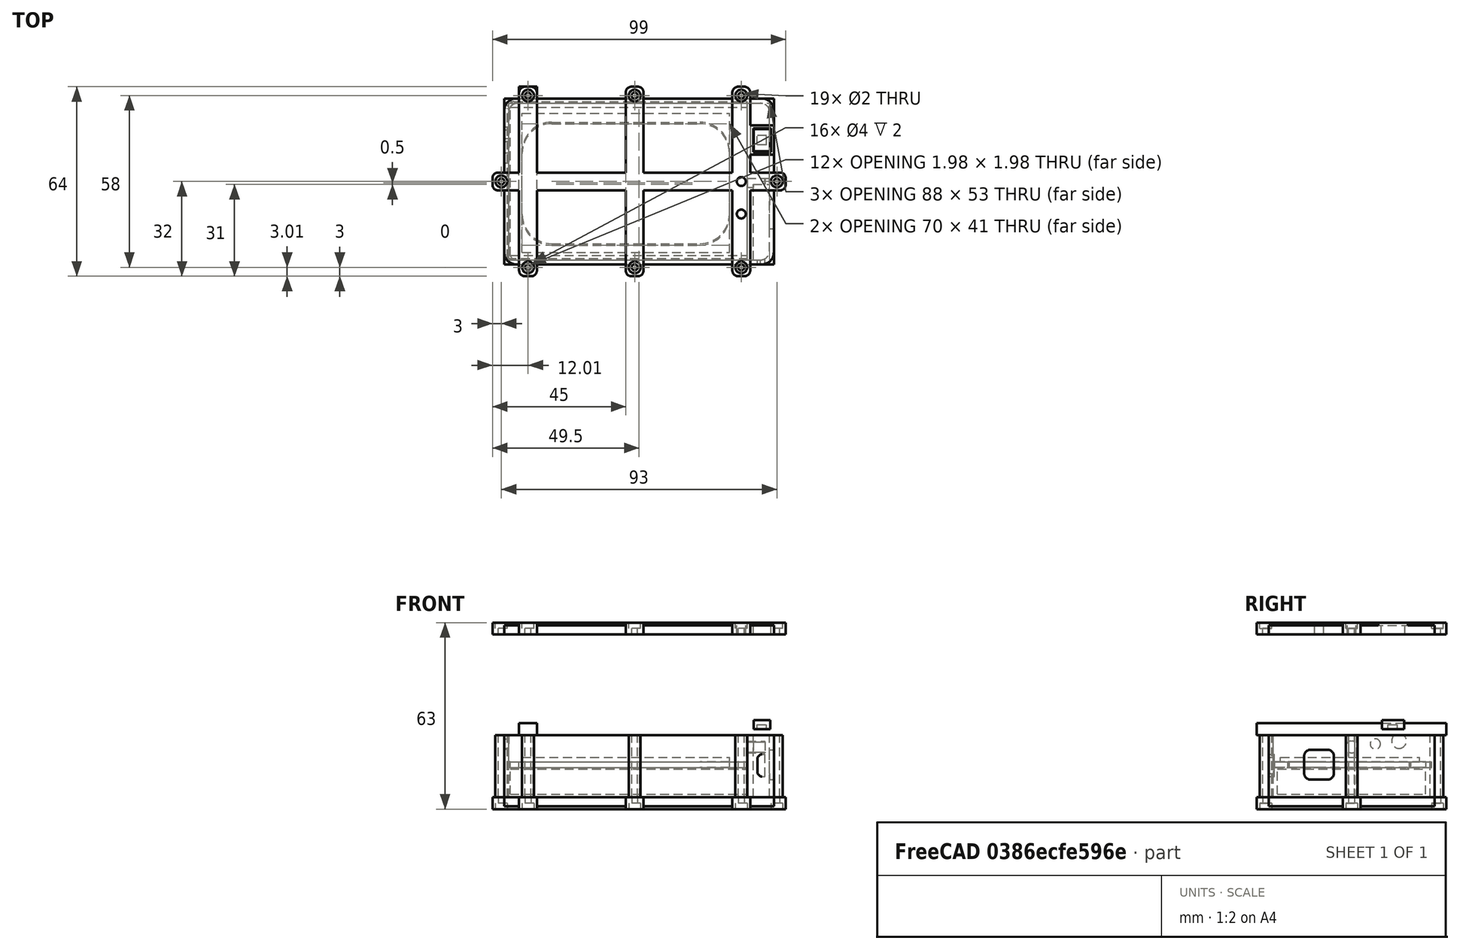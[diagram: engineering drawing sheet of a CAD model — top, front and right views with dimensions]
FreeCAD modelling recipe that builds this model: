
FCSTD DOCUMENT  (FreeCAD 0.20R29603 (Git))
Label: корпус
License: All rights reserved
LicenseURL: http://en.wikipedia.org/wiki/All_rights_reserved
objects: Part::Cylinder×43, Part::Fillet×35, Part::Cut×30, Part::Box×26, Part::MultiFuse×24, Part::FeaturePython×3, Part::Chamfer×1
note: 159 computed .brp shape members not serialized (recipe doc carries the construction recipe); baked Part::Feature solids carry a one-line shape summary decoded from their .brp

FEATURE [Part::Box] Box  label="Куб"
  AttacherType = Attacher::AttachEngine3D
  Height = 1.5
  Length = 70
  Placement = pos=(4,2,0) rot=(0,0,1;0rad)
  Width = 47
FEATURE [Part::Box] Box001  label="Куб001"
  AttacherType = Attacher::AttachEngine3D
  Height = 1.5
  Length = 17
  Width = 22
FEATURE [Part::Box] Box002  label="Куб002"
  AttacherType = Attacher::AttachEngine3D
  Height = 2.5
  Length = 7.5
  Placement = pos=(4.5,-4,1.5) rot=(0,0,1;0rad)
  Width = 11
FEATURE [Part::Chamfer] Chamfer
  Base = -> Box002
  Edges = 2 edges r=1: [Edge4,Edge8]
FEATURE [Part::MultiFuse] Fusion
  Placement = pos=(82,1,7) rot=(0,1,0;1.5708rad)
  Shapes = -> [Box001,Chamfer]
FEATURE [Part::Box] Box003  label="Куб003"
  AttacherType = Attacher::AttachEngine3D
  Height = 8.5
  Length = 80
  Placement = pos=(0,1,-11) rot=(0,0,1;0rad)
  Width = 50
FEATURE [Part::Box] Box004  label="Куб004"
  AttacherType = Attacher::AttachEngine3D
  Height = 21
  Length = 91
  Placement = pos=(-2,-2,-12) rot=(0,0,1;0rad)
  Width = 56
FEATURE [Part::Box] Box005  label="Куб005"
  AttacherType = Attacher::AttachEngine3D
  Height = 21
  Length = 88
  Placement = pos=(-0.5,-0.5,-12) rot=(0,0,1;0rad)
  Width = 53
FEATURE [Part::Cut] Cut
  Base = -> Box004
  Tool = -> Box005
FEATURE [Part::Box] Box006  label="Куб006"
  AttacherType = Attacher::AttachEngine3D
  Height = 21
  Length = 2
  Placement = pos=(80,-1,-12) rot=(0,0,1;0rad)
  Width = 26
FEATURE [Part::Box] Box007  label="Куб007"
  AttacherType = Attacher::AttachEngine3D
  Height = 21
  Length = 8
  Placement = pos=(80,25,-12) rot=(0,0,1;0rad)
  Width = 2
FEATURE [Part::Box] Box008  label="Куб008"
  AttacherType = Attacher::AttachEngine3D
  Height = 2
  Length = 81
  Placement = pos=(-1,0,-2) rot=(0,0,1;0rad)
  Width = 53
FEATURE [Part::Box] Box009  label="Куб009"
  AttacherType = Attacher::AttachEngine3D
  Height = 2
  Length = 70
  Placement = pos=(4,5,-2) rot=(0,0,1;0rad)
  Width = 41
FEATURE [Part::Fillet] Fillet
  Base = -> Box009
  Edges = 4 edges r=10: [Edge1,Edge3,Edge5,Edge7]
FEATURE [Part::Cut] Cut001
  Base = -> Box008
  Tool = -> Fillet
FEATURE [Part::Fillet] Fillet001
  Base = -> Cut
  Edges = 1 edges r=3: [Edge23]
FEATURE [Part::Fillet] Fillet002
  Base = -> Cut
  Edges = 1 edges r=3: [Edge23]
FEATURE [Part::Fillet] Fillet003
  Base = -> Fillet001
  Edges = 1 edges r=3: [Edge18]
FEATURE [Part::Fillet] Fillet004
  Base = -> Fillet001
  Edges = 1 edges r=3: [Edge18]
FEATURE [Part::Fillet] Fillet005
  Base = -> Fillet004
  Edges = 1 edges r=3: [Edge16]
FEATURE [Part::Fillet] Fillet006
  Base = -> Fillet005
  Edges = 1 edges r=3: [Edge20]
FEATURE [Part::Fillet] Fillet007
  Base = -> Fillet006
  Edges = 1 edges r=4: [Edge30]
FEATURE [Part::Fillet] Fillet008
  Base = -> Cut001
  Edges = 1 edges r=2.3: [Edge3]
FEATURE [Part::Fillet] Fillet009
  Base = -> Cut001
  Edges = 1 edges r=4: [Edge3]
  Placement = pos=(0,-0.5,0) rot=(0,0,1;0rad)
FEATURE [Part::Fillet] Fillet010
  Base = -> Fillet007
  Edges = 1 edges r=4: [Edge14]
FEATURE [Part::Fillet] Fillet011
  Base = -> Fillet007
  Edges = 1 edges r=4: [Edge14]
FEATURE [Part::Fillet] Fillet012
  Base = -> Fillet011
  Edges = 1 edges r=4: [Edge23]
FEATURE [Part::Fillet] Fillet013
  Base = -> Fillet012
  Edges = 1 edges r=4: [Edge24]
FEATURE [Part::Cut] Cut002
  Base = -> Fillet013
  Tool = -> Fusion
FEATURE [Part::Cylinder] Cylinder  label="Цилиндр"
  Angle = 360
  AttacherType = Attacher::AttachEngine3D
  FirstAngle = 0
  Height = 10
  Placement = pos=(-6,42,7) rot=(0,1,0;1.5708rad)
  Radius = 2.5
  SecondAngle = 0
FEATURE [Part::Cut] Cut003
  Base = -> Cut002
  Tool = -> Cylinder
FEATURE [Part::Cylinder] Cylinder001  label="Цилиндр001"
  Angle = 360
  AttacherType = Attacher::AttachEngine3D
  FirstAngle = 0
  Height = 10
  Placement = pos=(-4,34,6) rot=(0,1,0;1.5708rad)
  Radius = 1.75
  SecondAngle = 0
FEATURE [Part::Cut] Cut004
  Base = -> Cut003
  Tool = -> Cylinder001
FEATURE [Part::Box] Box010  label="Куб010"
  AttacherType = Attacher::AttachEngine3D
  Height = 10
  Length = 1.5
  Placement = pos=(87.5,10,-6) rot=(0,0,1;0rad)
  Width = 10
FEATURE [Part::MultiFuse] Fusion001
  Shapes = -> [Box006,Box007,Cut004,Fillet009]
FEATURE [Part::Fillet] Fillet014
  Base = -> Box010
  Edges = 4 edges r=2: [Edge9,Edge10,Edge11,Edge12]
FEATURE [Part::Box] Box011  label="Куб011"
  AttacherType = Attacher::AttachEngine3D
  Height = 10
  Length = 1.5
  Placement = pos=(87.5,10,-6) rot=(0,0,1;0rad)
  Width = 10
FEATURE [Part::Fillet] Fillet015
  Base = -> Box011
  Edges = 4 edges r=2: [Edge9,Edge10,Edge11,Edge12]
FEATURE [Part::Cut] Cut005
  Base = -> Fusion001
  Tool = -> Fillet014
FEATURE [Part::Cylinder] Cylinder002  label="Цилиндр002"
  Angle = 360
  AttacherType = Attacher::AttachEngine3D
  FirstAngle = 0
  Height = 10
  Placement = pos=(76,26,5) rot=(0,1,0;1.5708rad)
  Radius = 2
  SecondAngle = 0
FEATURE [Part::Cut] Cut006
  Base = -> Cut005
  Tool = -> Cylinder002
FEATURE [Part::Cylinder] Cylinder003  label="Цилиндр003"
  Angle = 360
  AttacherType = Attacher::AttachEngine3D
  FirstAngle = 0
  Height = 21
  Placement = pos=(6,-3,-12) rot=(0,0,1;0rad)
  Radius = 2
  SecondAngle = 0
FEATURE [Part::Cylinder] Cylinder004  label="Цилиндр004"
  Angle = 360
  AttacherType = Attacher::AttachEngine3D
  FirstAngle = 0
  Height = 21
  Placement = pos=(6,-3,-12) rot=(0,0,1;0rad)
  Radius = 1
  SecondAngle = 0
FEATURE [Part::Cut] Cut007
  Base = -> Cylinder003
  Tool = -> Cylinder004
FEATURE [Part::FeaturePython] Array  # Draft array (typed FeaturePython)
  AlwaysSyncPlacement = false
  Angle = 360
  ArrayType = 0
  Axis = (0,0,1)
  Base = -> Cut007
  Center = (0,0,0)
  Count = 3
  ExpandArray = false
  Fuse = false
  IntervalAxis = (0,0,0)
  IntervalX = (36,0,0)
  IntervalY = (0,100,0)
  IntervalZ = (0,0,100)
  NumberCircles = 3
  NumberPolar = 5
  NumberX = 3
  NumberY = 1
  NumberZ = 1
  PlacementList = 3 placements: arithmetic series from (0,0,0) step (36,0,0) to (72,0,0)
  RadialDistance = 50
  ScaleList = (3) [(1,1,1),(1,1,1),(1,1,1)]
  Symmetry = 1
  TangentialDistance = 25
FEATURE [Part::Cylinder] Cylinder005  label="Цилиндр005"
  Angle = 360
  AttacherType = Attacher::AttachEngine3D
  FirstAngle = 0
  Height = 21
  Placement = pos=(6,-3,-12) rot=(0,0,1;0rad)
  Radius = 1
  SecondAngle = 0
FEATURE [Part::Cylinder] Cylinder006  label="Цилиндр006"
  Angle = 360
  AttacherType = Attacher::AttachEngine3D
  FirstAngle = 0
  Height = 21
  Placement = pos=(6,-3,-12) rot=(0,0,1;0rad)
  Radius = 2
  SecondAngle = 0
FEATURE [Part::Cut] Cut008
  Base = -> Cylinder006
  Tool = -> Cylinder005
FEATURE [Part::FeaturePython] Array001  # Draft array (typed FeaturePython)
  AlwaysSyncPlacement = false
  Angle = 360
  ArrayType = 0
  Axis = (0,0,1)
  Base = -> Cut008
  Center = (0,0,0)
  Count = 3
  ExpandArray = false
  Fuse = false
  IntervalAxis = (0,0,0)
  IntervalX = (36,0,0)
  IntervalY = (0,100,0)
  IntervalZ = (0,0,100)
  NumberCircles = 3
  NumberPolar = 5
  NumberX = 3
  NumberY = 1
  NumberZ = 1
  Placement = pos=(0,58,0) rot=(0,0,1;0rad)
  PlacementList = 3 placements: arithmetic series from (0,0,0) step (36,0,0) to (72,0,0)
  RadialDistance = 50
  ScaleList = (3) [(1,1,1),(1,1,1),(1,1,1)]
  Symmetry = 1
  TangentialDistance = 25
FEATURE [Part::Cylinder] Cylinder007  label="Цилиндр007"
  Angle = 360
  AttacherType = Attacher::AttachEngine3D
  FirstAngle = 0
  Height = 21
  Placement = pos=(6,-3,-12) rot=(0,0,1;0rad)
  Radius = 1
  SecondAngle = 0
FEATURE [Part::Cylinder] Cylinder008  label="Цилиндр008"
  Angle = 360
  AttacherType = Attacher::AttachEngine3D
  FirstAngle = 0
  Height = 21
  Placement = pos=(6,-3,-12) rot=(0,0,1;0rad)
  Radius = 2
  SecondAngle = 0
FEATURE [Part::Cut] Cut009
  Base = -> Cylinder008
  Placement = pos=(-9,29,0) rot=(0,0,1;0rad)
  Tool = -> Cylinder007
FEATURE [Part::FeaturePython] Array002  # Draft array (typed FeaturePython)
  AlwaysSyncPlacement = false
  Angle = 360
  ArrayType = 0
  Axis = (0,0,1)
  Base = -> Cut009
  Center = (0,0,0)
  Count = 2
  ExpandArray = false
  Fuse = false
  IntervalAxis = (0,0,0)
  IntervalX = (93,0,0)
  IntervalY = (0,100,0)
  IntervalZ = (0,0,100)
  NumberCircles = 3
  NumberPolar = 5
  NumberX = 2
  NumberY = 1
  NumberZ = 1
  PlacementList = 2 placements: [(-9,29,0),(84,29,0)]
  RadialDistance = 50
  ScaleList = (2) [(1,1,1),(1,1,1)]
  Symmetry = 1
  TangentialDistance = 25
FEATURE [Part::MultiFuse] Fusion002
  Shapes = -> [Cut006,Array,Array001,Array002]
FEATURE [Part::Box] Box012  label="Куб012"
  AttacherType = Attacher::AttachEngine3D
  Height = 3
  Length = 91
  Placement = pos=(-2,-2,9) rot=(0,0,1;0rad)
  Width = 56
FEATURE [Part::Fillet] Fillet016
  Base = -> Box012
  Edges = 4 edges r=4: [Edge1,Edge3,Edge5,Edge7]
FEATURE [Part::Box] Box013  label="Куб013"
  AttacherType = Attacher::AttachEngine3D
  Height = 4
  Length = 6
  Placement = pos=(3,-6,9) rot=(0,0,1;0rad)
  Width = 64
FEATURE [Part::Fillet] Fillet017
  Base = -> Box013
  Edges = 2 edges r=1.9: [Edge1,Edge5]
FEATURE [Part::Fillet] Fillet018
  Base = -> Box013
  Edges = 2 edges r=1.9: [Edge1,Edge5]
FEATURE [Part::Fillet] Fillet019
  Base = -> Fillet018
  Edges = 2 edges r=1.9: [Edge4,Edge13]
FEATURE [Part::Box] Box014  label="Куб014"
  AttacherType = Attacher::AttachEngine3D
  Height = 4
  Length = 6
  Placement = pos=(3,-6,9) rot=(0,0,1;0rad)
  Width = 64
FEATURE [Part::Fillet] Fillet021
  Base = -> Box014
  Edges = 2 edges r=1.9: [Edge1,Edge5]
FEATURE [Part::Fillet] Fillet020
  Base = -> Fillet021
  Edges = 2 edges r=1.9: [Edge4,Edge13]
  Placement = pos=(36,0,0) rot=(0,0,1;0rad)
FEATURE [Part::Box] Box015  label="Куб015"
  AttacherType = Attacher::AttachEngine3D
  Height = 4
  Length = 6
  Placement = pos=(3,-6,9) rot=(0,0,1;0rad)
  Width = 64
FEATURE [Part::Fillet] Fillet022
  Base = -> Box015
  Edges = 2 edges r=1.9: [Edge1,Edge5]
FEATURE [Part::Fillet] Fillet023
  Base = -> Fillet022
  Edges = 2 edges r=1.9: [Edge4,Edge13]
  Placement = pos=(72,0,0) rot=(0,0,1;0rad)
FEATURE [Part::Box] Box016  label="Куб016"
  AttacherType = Attacher::AttachEngine3D
  Height = 4
  Length = 6
  Placement = pos=(3,-6,9) rot=(0,0,1;0rad)
  Width = 99
FEATURE [Part::Fillet] Fillet024
  Base = -> Box016
  Edges = 2 edges r=1.9: [Edge1,Edge5]
FEATURE [Part::Fillet] Fillet025
  Base = -> Fillet024
  Edges = 2 edges r=1.9: [Edge4,Edge13]
  Placement = pos=(87,20,0) rot=(0,0,1;1.5708rad)
FEATURE [Part::Cylinder] Cylinder009  label="Цилиндр009"
  Angle = 360
  AttacherType = Attacher::AttachEngine3D
  FirstAngle = 0
  Height = 10
  Placement = pos=(6,-3,5) rot=(0,0,1;0rad)
  Radius = 1
  SecondAngle = 0
FEATURE [Part::Cylinder] Cylinder010  label="Цилиндр010"
  Angle = 360
  AttacherType = Attacher::AttachEngine3D
  FirstAngle = 0
  Height = 2
  Placement = pos=(6,-3,11) rot=(0,0,1;0rad)
  Radius = 2
  SecondAngle = 0
FEATURE [Part::MultiFuse] Fusion003
  Shapes = -> [Cylinder009,Cylinder010]
FEATURE [Part::Cylinder] Cylinder011  label="Цилиндр011"
  Angle = 360
  AttacherType = Attacher::AttachEngine3D
  FirstAngle = 0
  Height = 2
  Placement = pos=(6,-3,11) rot=(0,0,1;0rad)
  Radius = 2
  SecondAngle = 0
FEATURE [Part::Cylinder] Cylinder012  label="Цилиндр012"
  Angle = 360
  AttacherType = Attacher::AttachEngine3D
  FirstAngle = 0
  Height = 10
  Placement = pos=(6,-3,5) rot=(0,0,1;0rad)
  Radius = 1
  SecondAngle = 0
FEATURE [Part::MultiFuse] Fusion004
  Placement = pos=(36,0,0) rot=(0,0,1;0rad)
  Shapes = -> [Cylinder012,Cylinder011]
FEATURE [Part::Cylinder] Cylinder013  label="Цилиндр013"
  Angle = 360
  AttacherType = Attacher::AttachEngine3D
  FirstAngle = 0
  Height = 2
  Placement = pos=(6,-3,11) rot=(0,0,1;0rad)
  Radius = 2
  SecondAngle = 0
FEATURE [Part::Cylinder] Cylinder014  label="Цилиндр014"
  Angle = 360
  AttacherType = Attacher::AttachEngine3D
  FirstAngle = 0
  Height = 10
  Placement = pos=(6,-3,5) rot=(0,0,1;0rad)
  Radius = 1
  SecondAngle = 0
FEATURE [Part::MultiFuse] Fusion005
  Placement = pos=(72,0,0) rot=(0,0,1;0rad)
  Shapes = -> [Cylinder014,Cylinder013]
FEATURE [Part::Cylinder] Cylinder015  label="Цилиндр015"
  Angle = 360
  AttacherType = Attacher::AttachEngine3D
  FirstAngle = 0
  Height = 2
  Placement = pos=(6,-3,11) rot=(0,0,1;0rad)
  Radius = 2
  SecondAngle = 0
FEATURE [Part::Cylinder] Cylinder016  label="Цилиндр016"
  Angle = 360
  AttacherType = Attacher::AttachEngine3D
  FirstAngle = 0
  Height = 10
  Placement = pos=(6,-3,5) rot=(0,0,1;0rad)
  Radius = 1
  SecondAngle = 0
FEATURE [Part::Cylinder] Cylinder017  label="Цилиндр017"
  Angle = 360
  AttacherType = Attacher::AttachEngine3D
  FirstAngle = 0
  Height = 2
  Placement = pos=(6,-3,11) rot=(0,0,1;0rad)
  Radius = 2
  SecondAngle = 0
FEATURE [Part::Cylinder] Cylinder018  label="Цилиндр018"
  Angle = 360
  AttacherType = Attacher::AttachEngine3D
  FirstAngle = 0
  Height = 10
  Placement = pos=(6,-3,5) rot=(0,0,1;0rad)
  Radius = 1
  SecondAngle = 0
FEATURE [Part::MultiFuse] Fusion006
  Placement = pos=(36,58,0) rot=(0,0,1;0rad)
  Shapes = -> [Cylinder018,Cylinder017]
FEATURE [Part::Cylinder] Cylinder019  label="Цилиндр019"
  Angle = 360
  AttacherType = Attacher::AttachEngine3D
  FirstAngle = 0
  Height = 10
  Placement = pos=(6,-3,5) rot=(0,0,1;0rad)
  Radius = 1
  SecondAngle = 0
FEATURE [Part::MultiFuse] Fusion007
  Placement = pos=(0,58,0) rot=(0,0,1;0rad)
  Shapes = -> [Cylinder019,Cylinder015]
FEATURE [Part::Cylinder] Cylinder020  label="Цилиндр020"
  Angle = 360
  AttacherType = Attacher::AttachEngine3D
  FirstAngle = 0
  Height = 2
  Placement = pos=(6,-3,11) rot=(0,0,1;0rad)
  Radius = 2
  SecondAngle = 0
FEATURE [Part::MultiFuse] Fusion008
  Placement = pos=(72,58,0) rot=(0,0,1;0rad)
  Shapes = -> [Cylinder016,Cylinder020]
FEATURE [Part::Cylinder] Cylinder021  label="Цилиндр021"
  Angle = 360
  AttacherType = Attacher::AttachEngine3D
  FirstAngle = 0
  Height = 2
  Placement = pos=(6,-3,11) rot=(0,0,1;0rad)
  Radius = 2
  SecondAngle = 0
FEATURE [Part::Cylinder] Cylinder022  label="Цилиндр022"
  Angle = 360
  AttacherType = Attacher::AttachEngine3D
  FirstAngle = 0
  Height = 10
  Placement = pos=(6,-3,5) rot=(0,0,1;0rad)
  Radius = 1
  SecondAngle = 0
FEATURE [Part::MultiFuse] Fusion009
  Placement = pos=(84,29,0) rot=(0,0,1;0rad)
  Shapes = -> [Cylinder022,Cylinder021]
FEATURE [Part::Cylinder] Cylinder023  label="Цилиндр023"
  Angle = 360
  AttacherType = Attacher::AttachEngine3D
  FirstAngle = 0
  Height = 2
  Placement = pos=(6,-3,11) rot=(0,0,1;0rad)
  Radius = 2
  SecondAngle = 0
FEATURE [Part::Cylinder] Cylinder024  label="Цилиндр024"
  Angle = 360
  AttacherType = Attacher::AttachEngine3D
  FirstAngle = 0
  Height = 10
  Placement = pos=(6,-3,5) rot=(0,0,1;0rad)
  Radius = 1
  SecondAngle = 0
FEATURE [Part::MultiFuse] Fusion010
  Placement = pos=(-9,29,0) rot=(0,0,1;0rad)
  Shapes = -> [Cylinder024,Cylinder023]
FEATURE [Part::MultiFuse] Fusion011
  Shapes = -> [Fillet025,Fillet023,Fillet020,Fillet019]
FEATURE [Part::MultiFuse] Fusion012
  Shapes = -> [Fillet016,Fusion011]
FEATURE [Part::Cut] Cut010
  Base = -> Fusion012
  Tool = -> Fusion010
FEATURE [Part::Cut] Cut011
  Base = -> Cut010
  Tool = -> Fusion009
FEATURE [Part::Cut] Cut012
  Base = -> Cut011
  Tool = -> Fusion008
FEATURE [Part::Cut] Cut013
  Base = -> Cut012
  Tool = -> Fusion007
FEATURE [Part::Cut] Cut014
  Base = -> Cut013
  Tool = -> Fusion006
FEATURE [Part::Cut] Cut015
  Base = -> Cut014
  Tool = -> Fusion005
FEATURE [Part::Cut] Cut016
  Base = -> Cut015
  Tool = -> Fusion004
FEATURE [Part::Cut] Cut017
  Base = -> Cut016
  Tool = -> Fusion003
FEATURE [Part::Box] Box017  label="Куб017"
  AttacherType = Attacher::AttachEngine3D
  Height = 4
  Length = 6
  Placement = pos=(3,-6,9) rot=(0,0,1;0rad)
  Width = 64
FEATURE [Part::Fillet] Fillet026
  Base = -> Box017
  Edges = 2 edges r=1.9: [Edge1,Edge5]
FEATURE [Part::Box] Box018  label="Куб018"
  AttacherType = Attacher::AttachEngine3D
  Height = 4
  Length = 6
  Placement = pos=(3,-6,9) rot=(0,0,1;0rad)
  Width = 64
FEATURE [Part::Box] Box019  label="Куб019"
  AttacherType = Attacher::AttachEngine3D
  Height = 3
  Length = 91
  Placement = pos=(-2,-2,9) rot=(0,0,1;0rad)
  Width = 56
FEATURE [Part::Fillet] Fillet028
  Base = -> Box019
  Edges = 4 edges r=4: [Edge1,Edge3,Edge5,Edge7]
FEATURE [Part::Fillet] Fillet030
  Base = -> Box018
  Edges = 2 edges r=1.9: [Edge1,Edge5]
FEATURE [Part::Fillet] Fillet027
  Base = -> Fillet030
  Edges = 2 edges r=1.9: [Edge4,Edge13]
FEATURE [Part::Fillet] Fillet031
  Base = -> Fillet026
  Edges = 2 edges r=1.9: [Edge4,Edge13]
  Placement = pos=(36,0,0) rot=(0,0,1;0rad)
FEATURE [Part::Cylinder] Cylinder025  label="Цилиндр025"
  Angle = 360
  AttacherType = Attacher::AttachEngine3D
  FirstAngle = 0
  Height = 2
  Placement = pos=(6,-3,11) rot=(0,0,1;0rad)
  Radius = 2
  SecondAngle = 0
FEATURE [Part::Cylinder] Cylinder026  label="Цилиндр026"
  Angle = 360
  AttacherType = Attacher::AttachEngine3D
  FirstAngle = 0
  Height = 2
  Placement = pos=(6,-3,11) rot=(0,0,1;0rad)
  Radius = 2
  SecondAngle = 0
FEATURE [Part::Cylinder] Cylinder027  label="Цилиндр027"
  Angle = 360
  AttacherType = Attacher::AttachEngine3D
  FirstAngle = 0
  Height = 10
  Placement = pos=(6,-3,5) rot=(0,0,1;0rad)
  Radius = 1
  SecondAngle = 0
FEATURE [Part::MultiFuse] Fusion017
  Placement = pos=(84,29,0) rot=(0,0,1;0rad)
  Shapes = -> [Cylinder027,Cylinder025]
FEATURE [Part::Cylinder] Cylinder028  label="Цилиндр028"
  Angle = 360
  AttacherType = Attacher::AttachEngine3D
  FirstAngle = 0
  Height = 2
  Placement = pos=(6,-3,11) rot=(0,0,1;0rad)
  Radius = 2
  SecondAngle = 0
FEATURE [Part::Cylinder] Cylinder029  label="Цилиндр029"
  Angle = 360
  AttacherType = Attacher::AttachEngine3D
  FirstAngle = 0
  Height = 10
  Placement = pos=(6,-3,5) rot=(0,0,1;0rad)
  Radius = 1
  SecondAngle = 0
FEATURE [Part::MultiFuse] Fusion014
  Placement = pos=(-9,29,0) rot=(0,0,1;0rad)
  Shapes = -> [Cylinder029,Cylinder028]
FEATURE [Part::Cylinder] Cylinder030  label="Цилиндр030"
  Angle = 360
  AttacherType = Attacher::AttachEngine3D
  FirstAngle = 0
  Height = 2
  Placement = pos=(6,-3,11) rot=(0,0,1;0rad)
  Radius = 2
  SecondAngle = 0
FEATURE [Part::Cylinder] Cylinder031  label="Цилиндр031"
  Angle = 360
  AttacherType = Attacher::AttachEngine3D
  FirstAngle = 0
  Height = 10
  Placement = pos=(6,-3,5) rot=(0,0,1;0rad)
  Radius = 1
  SecondAngle = 0
FEATURE [Part::Box] Box020  label="Куб020"
  AttacherType = Attacher::AttachEngine3D
  Height = 4
  Length = 6
  Placement = pos=(3,-6,9) rot=(0,0,1;0rad)
  Width = 99
FEATURE [Part::Fillet] Fillet034
  Base = -> Box020
  Edges = 2 edges r=1.9: [Edge1,Edge5]
FEATURE [Part::Fillet] Fillet033
  Base = -> Fillet034
  Edges = 2 edges r=1.9: [Edge4,Edge13]
  Placement = pos=(87,20,0) rot=(0,0,1;1.5708rad)
FEATURE [Part::Cylinder] Cylinder032  label="Цилиндр032"
  Angle = 360
  AttacherType = Attacher::AttachEngine3D
  FirstAngle = 0
  Height = 2
  Placement = pos=(6,-3,11) rot=(0,0,1;0rad)
  Radius = 2
  SecondAngle = 0
FEATURE [Part::Cylinder] Cylinder033  label="Цилиндр033"
  Angle = 360
  AttacherType = Attacher::AttachEngine3D
  FirstAngle = 0
  Height = 10
  Placement = pos=(6,-3,5) rot=(0,0,1;0rad)
  Radius = 1
  SecondAngle = 0
FEATURE [Part::MultiFuse] Fusion018
  Placement = pos=(36,0,0) rot=(0,0,1;0rad)
  Shapes = -> [Cylinder033,Cylinder032]
FEATURE [Part::Cylinder] Cylinder034  label="Цилиндр034"
  Angle = 360
  AttacherType = Attacher::AttachEngine3D
  FirstAngle = 0
  Height = 10
  Placement = pos=(6,-3,5) rot=(0,0,1;0rad)
  Radius = 1
  SecondAngle = 0
FEATURE [Part::MultiFuse] Fusion019
  Shapes = -> [Cylinder034,Cylinder030]
FEATURE [Part::Cylinder] Cylinder035  label="Цилиндр035"
  Angle = 360
  AttacherType = Attacher::AttachEngine3D
  FirstAngle = 0
  Height = 2
  Placement = pos=(6,-3,11) rot=(0,0,1;0rad)
  Radius = 2
  SecondAngle = 0
FEATURE [Part::MultiFuse] Fusion022
  Placement = pos=(72,0,0) rot=(0,0,1;0rad)
  Shapes = -> [Cylinder031,Cylinder035]
FEATURE [Part::Cylinder] Cylinder036  label="Цилиндр036"
  Angle = 360
  AttacherType = Attacher::AttachEngine3D
  FirstAngle = 0
  Height = 2
  Placement = pos=(6,-3,11) rot=(0,0,1;0rad)
  Radius = 2
  SecondAngle = 0
FEATURE [Part::Cylinder] Cylinder037  label="Цилиндр037"
  Angle = 360
  AttacherType = Attacher::AttachEngine3D
  FirstAngle = 0
  Height = 10
  Placement = pos=(6,-3,5) rot=(0,0,1;0rad)
  Radius = 1
  SecondAngle = 0
FEATURE [Part::MultiFuse] Fusion015
  Placement = pos=(72,58,0) rot=(0,0,1;0rad)
  Shapes = -> [Cylinder037,Cylinder026]
FEATURE [Part::Cylinder] Cylinder038  label="Цилиндр038"
  Angle = 360
  AttacherType = Attacher::AttachEngine3D
  FirstAngle = 0
  Height = 10
  Placement = pos=(6,-3,5) rot=(0,0,1;0rad)
  Radius = 1
  SecondAngle = 0
FEATURE [Part::Cylinder] Cylinder039  label="Цилиндр039"
  Angle = 360
  AttacherType = Attacher::AttachEngine3D
  FirstAngle = 0
  Height = 2
  Placement = pos=(6,-3,11) rot=(0,0,1;0rad)
  Radius = 2
  SecondAngle = 0
FEATURE [Part::MultiFuse] Fusion020
  Placement = pos=(36,58,0) rot=(0,0,1;0rad)
  Shapes = -> [Cylinder038,Cylinder039]
FEATURE [Part::Box] Box021  label="Куб021"
  AttacherType = Attacher::AttachEngine3D
  Height = 4
  Length = 6
  Placement = pos=(3,-6,9) rot=(0,0,1;0rad)
  Width = 64
FEATURE [Part::Fillet] Fillet029
  Base = -> Box021
  Edges = 2 edges r=1.9: [Edge1,Edge5]
FEATURE [Part::Fillet] Fillet032
  Base = -> Fillet029
  Edges = 2 edges r=1.9: [Edge4,Edge13]
  Placement = pos=(72,0,0) rot=(0,0,1;0rad)
FEATURE [Part::MultiFuse] Fusion016
  Shapes = -> [Fillet033,Fillet032,Fillet031,Fillet027]
FEATURE [Part::MultiFuse] Fusion013
  Shapes = -> [Fillet028,Fusion016]
FEATURE [Part::Cut] Cut020
  Base = -> Fusion013
  Tool = -> Fusion014
FEATURE [Part::Cut] Cut025
  Base = -> Cut020
  Tool = -> Fusion017
FEATURE [Part::Cut] Cut022
  Base = -> Cut025
  Tool = -> Fusion015
FEATURE [Part::Cylinder] Cylinder040  label="Цилиндр040"
  Angle = 360
  AttacherType = Attacher::AttachEngine3D
  FirstAngle = 0
  Height = 10
  Placement = pos=(6,-3,5) rot=(0,0,1;0rad)
  Radius = 1
  SecondAngle = 0
FEATURE [Part::MultiFuse] Fusion021
  Placement = pos=(0,58,0) rot=(0,0,1;0rad)
  Shapes = -> [Cylinder040,Cylinder036]
FEATURE [Part::Cut] Cut019
  Base = -> Cut022
  Tool = -> Fusion021
FEATURE [Part::Cut] Cut024
  Base = -> Cut019
  Tool = -> Fusion020
FEATURE [Part::Cut] Cut023
  Base = -> Cut024
  Tool = -> Fusion022
FEATURE [Part::Cut] Cut021
  Base = -> Cut023
  Tool = -> Fusion018
FEATURE [Part::Cut] Cut018
  Base = -> Cut021
  Placement = pos=(0,52,-3) rot=(1,0,0;3.14159rad)
  Tool = -> Fusion019
FEATURE [Part::Cylinder] Cylinder041  label="Цилиндр041"
  Angle = 360
  AttacherType = Attacher::AttachEngine3D
  FirstAngle = 0
  Height = 10
  Placement = pos=(78,15,3) rot=(0,0,1;0rad)
  Radius = 1.5
  SecondAngle = 0
FEATURE [Part::Cylinder] Cylinder042  label="Цилиндр042"
  Angle = 360
  AttacherType = Attacher::AttachEngine3D
  FirstAngle = 0
  Height = 10
  Placement = pos=(78,26,3) rot=(0,0,1;0rad)
  Radius = 1.5
  SecondAngle = 0
FEATURE [Part::Cut] Cut026
  Base = -> Cut017
  Tool = -> Cylinder041
FEATURE [Part::Cut] Cut027
  Base = -> Cut026
  Tool = -> Cylinder042
FEATURE [Part::Box] Box022  label="Куб022"
  AttacherType = Attacher::AttachEngine3D
  Height = 4
  Length = 8
  Placement = pos=(81,35,9) rot=(0,0,1;0rad)
  Width = 10
FEATURE [Part::Box] Box023  label="Куб023"
  AttacherType = Attacher::AttachEngine3D
  Height = 4
  Length = 6
  Placement = pos=(82,36,9) rot=(0,0,1;0rad)
  Width = 8
FEATURE [Part::MultiFuse] Fusion023
  Shapes = -> [Box022,Cut027]
FEATURE [Part::Cut] Cut028
  Base = -> Fusion023
  Placement = pos=(0,0,34) rot=(0,0,1;0rad)
  Tool = -> Box023
FEATURE [Part::Box] Box024  label="Куб024"
  AttacherType = Attacher::AttachEngine3D
  Height = 3
  Length = 5.5
  Placement = pos=(82.25,36.25,18) rot=(0,0,1;0rad)
  Width = 7.5
FEATURE [Part::Box] Box025  label="Куб025"
  AttacherType = Attacher::AttachEngine3D
  Height = 3
  Length = 3.2
  Placement = pos=(83.3,38.3,16.5) rot=(0,0,1;0rad)
  Width = 3.2
FEATURE [Part::Cut] Cut029
  Base = -> Box024
  Placement = pos=(0,0,-7) rot=(0,0,1;0rad)
  Tool = -> Box025
